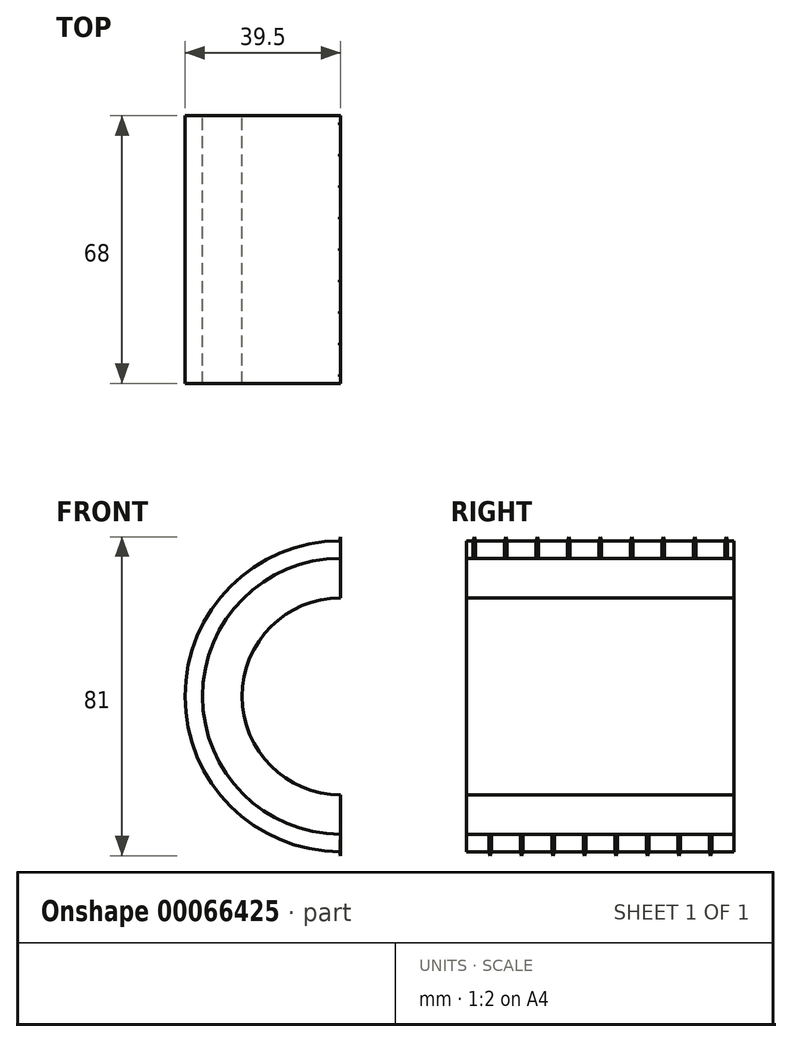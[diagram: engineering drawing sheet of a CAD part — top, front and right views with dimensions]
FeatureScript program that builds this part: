
annotation { "Feature Type Name" : "Feature", "Feature Type Description" : "" }
export const myFeature = defineFeature(function(context is Context, id is Id, definition is map)
    precondition{}
    {
        {
            var Q0;
            Q0=qCreatedBy(makeId("Front.planeOp"),FACE);
            var sketch = newSketch(context, id + "F0", { "sketchPlane" : qUnion([Q0])});
            skCircle(sketch, "E0", {"center": v(0, 0) * mm, "radius": 25.02 * mm});
            skCircle(sketch, "E1", {"center": v(0, 0) * mm, "radius": 35.05 * mm});
            skSolve(sketch);
        }
        {
            var Q0;
            Q0=makeQuery(id+"F0.imprint","IMPRINT",FACE,{"disambiguationData":[TD([[makeQuery(id+"F0.imprint","IMPRINT",EDGE,{"derivedFrom":sQuery(id+"F0.wireOp",EDGE,"E0")}),-1.0]])]});
            extrude(context, id + "F1", {"entities" : qUnion([Q0]), "endBound" : BoundingType.SYMMETRIC, "depth" : 68 * mm});
        }
        {
            var Q0;
            Q0=qCreatedBy(makeId("Front.planeOp"),FACE);
            var sketch = newSketch(context, id + "F2", { "sketchPlane" : qUnion([Q0])});
            skCircle(sketch, "E2.0", {"center": v(0, 0) * mm, "radius": 35.05 * mm});
            skCircle(sketch, "E3", {"center": v(0, 0) * mm, "radius": 39.5 * mm});
            skSolve(sketch);
        }
        {
            var Q0;
            Q0=makeQuery(id+"F2.imprint","IMPRINT",FACE,{"disambiguationData":[TD([[makeQuery(id+"F2.imprint","IMPRINT",EDGE,{"derivedFrom":sQuery(id+"F2.wireOp",EDGE,"E2.0")}),-1.0]])]});
            extrude(context, id + "F3", {"entities" : qUnion([Q0]), "endBound" : BoundingType.SYMMETRIC, "depth" : 68 * mm});
        }
        {
            var Q0;
            Q0=qCreatedBy(makeId("Top.planeOp"),FACE);
            cPlane(context, id + "F4", {"entities" : qUnion([Q0]), "cplaneType" : CPlaneType.OFFSET, "offset" : 70.1 / 2 * mm, "width" : 152.4 * mm, "height" : 152.4 * mm});
        }
        {
            var Q0;
            Q0=qCreatedBy(id+"F4.planeOp",FACE);
            var sketch = newSketch(context, id + "F5", { "sketchPlane" : qUnion([Q0])});
            skCircle(sketch, "E4", {"center": v(0, 0) * mm, "radius": 0.31 * mm});
            skCircle(sketch, "E5.0.1.0", {"center": v(0, 8) * mm, "radius": 0.31 * mm});
            skCircle(sketch, "E5.0.2.0", {"center": v(0, 16) * mm, "radius": 0.31 * mm});
            skCircle(sketch, "E5.0.3.0", {"center": v(0, 24) * mm, "radius": 0.31 * mm});
            skCircle(sketch, "E5.0.4.0", {"center": v(0, 32) * mm, "radius": 0.31 * mm});
            skLineSegment(sketch, "E5.direction1", {"start": v(0, 0) * mm, "end": v(25.4, 0) * mm, "construction": true});
            skLineSegment(sketch, "E5.direction2", {"start": v(0, 0) * mm, "end": v(0, 8) * mm, "construction": true});
            skCircle(sketch, "E6.0.1.0", {"center": v(0, -8) * mm, "radius": 0.31 * mm});
            skCircle(sketch, "E6.0.2.0", {"center": v(0, -16) * mm, "radius": 0.31 * mm});
            skCircle(sketch, "E6.0.3.0", {"center": v(0, -24) * mm, "radius": 0.31 * mm});
            skCircle(sketch, "E6.0.4.0", {"center": v(0, -32) * mm, "radius": 0.31 * mm});
            skLineSegment(sketch, "E6.direction2", {"start": v(0, 0) * mm, "end": v(0, -8) * mm, "construction": true});
            skSolve(sketch);
        }
        {
            var Q0;
            Q0=qSketchRegion(id+"F5",true);
            extrude(context, id + "F6", {"entities" : qUnion([Q0]), "operationType" : NewBodyOperationType.REMOVE, "depth" : 25.4 * mm});
        }
        {
            var Q0;
            Q0=qSketchRegion(id+"F5",true);
            extrude(context, id + "F7", {"entities" : qUnion([Q0]), "depth" : 5.45 * mm});
        }
        {
            var Q0;
            Q0=makeQuery(id+"F7.opExtrude","CAP_EDGE",EDGE,{"disambiguationData":[OSD([sQuery(id+"F5.wireOp",EDGE,"E6.0.4.0")])],"isStart":false});
            var Q1;
            Q1=makeQuery(id+"F7.opExtrude","CAP_EDGE",EDGE,{"disambiguationData":[OSD([sQuery(id+"F5.wireOp",EDGE,"E6.0.3.0")])],"isStart":false});
            var Q2;
            Q2=makeQuery(id+"F7.opExtrude","CAP_EDGE",EDGE,{"disambiguationData":[OSD([sQuery(id+"F5.wireOp",EDGE,"E6.0.2.0")])],"isStart":false});
            var Q3;
            Q3=makeQuery(id+"F7.opExtrude","CAP_EDGE",EDGE,{"disambiguationData":[OSD([sQuery(id+"F5.wireOp",EDGE,"E6.0.1.0")])],"isStart":false});
            var Q4;
            Q4=makeQuery(id+"F7.opExtrude","CAP_EDGE",EDGE,{"disambiguationData":[OSD([sQuery(id+"F5.wireOp",EDGE,"E4")])],"isStart":false});
            var Q5;
            Q5=makeQuery(id+"F7.opExtrude","CAP_EDGE",EDGE,{"disambiguationData":[OSD([sQuery(id+"F5.wireOp",EDGE,"E5.0.1.0")])],"isStart":false});
            var Q6;
            Q6=makeQuery(id+"F7.opExtrude","CAP_EDGE",EDGE,{"disambiguationData":[OSD([sQuery(id+"F5.wireOp",EDGE,"E5.0.2.0")])],"isStart":false});
            var Q7;
            Q7=makeQuery(id+"F7.opExtrude","CAP_EDGE",EDGE,{"disambiguationData":[OSD([sQuery(id+"F5.wireOp",EDGE,"E5.0.3.0")])],"isStart":false});
            var Q8;
            Q8=makeQuery(id+"F7.opExtrude","CAP_EDGE",EDGE,{"disambiguationData":[OSD([sQuery(id+"F5.wireOp",EDGE,"E5.0.4.0")])],"isStart":false});
            chamfer(context, id + "F8", {"entities" : qUnion([Q0, Q1, Q2, Q3, Q4, Q5, Q6, Q7, Q8]), "chamferType" : ChamferType.TWO_OFFSETS, "width1" : 0.31 * mm, "oppositeDirection" : false, "width2" : 1 * mm});
        }
        {
            var Q0;
            Q0=qCreatedBy(makeId("Top.planeOp"),FACE);
            cPlane(context, id + "F9", {"entities" : qUnion([Q0]), "cplaneType" : CPlaneType.OFFSET, "offset" : 70.1 * mm / 2, "oppositeDirection" : true, "width" : 152.4 * mm, "height" : 152.4 * mm});
        }
        {
            var Q0;
            Q0=qCreatedBy(id+"F9.planeOp",FACE);
            var sketch = newSketch(context, id + "F10", { "sketchPlane" : qUnion([Q0])});
            skCircle(sketch, "E7", {"center": v(0, -4) * mm, "radius": 0.31 * mm});
            skCircle(sketch, "E8", {"center": v(0, 4) * mm, "radius": 0.31 * mm});
            skCircle(sketch, "E9.0.1.0", {"center": v(0, -12) * mm, "radius": 0.31 * mm});
            skCircle(sketch, "E9.0.2.0", {"center": v(0, -20) * mm, "radius": 0.31 * mm});
            skCircle(sketch, "E9.0.3.0", {"center": v(0, -28) * mm, "radius": 0.31 * mm});
            skLineSegment(sketch, "E9.direction1", {"start": v(0, -4) * mm, "end": v(20.95, -4) * mm, "construction": true});
            skLineSegment(sketch, "E9.direction2", {"start": v(0, -4) * mm, "end": v(0, -12) * mm, "construction": true});
            skCircle(sketch, "E10.0.1.0", {"center": v(0, 12) * mm, "radius": 0.31 * mm});
            skCircle(sketch, "E10.0.2.0", {"center": v(0, 20) * mm, "radius": 0.31 * mm});
            skCircle(sketch, "E10.0.3.0", {"center": v(0, 28) * mm, "radius": 0.31 * mm});
            skLineSegment(sketch, "E10.direction1", {"start": v(0, 4) * mm, "end": v(25.4, 4) * mm, "construction": true});
            skLineSegment(sketch, "E10.direction2", {"start": v(0, 4) * mm, "end": v(0, 12) * mm, "construction": true});
            skSolve(sketch);
        }
        {
            var Q0;
            Q0=qSketchRegion(id+"F10",true);
            extrude(context, id + "F11", {"entities" : qUnion([Q0]), "operationType" : NewBodyOperationType.REMOVE, "oppositeDirection" : true, "depth" : 25.4 * mm});
        }
        {
            var Q0;
            Q0=qSketchRegion(id+"F10",true);
            extrude(context, id + "F12", {"entities" : qUnion([Q0]), "oppositeDirection" : true, "depth" : 5.45 * mm});
        }
        {
            var Q0;
            Q0=makeQuery(id+"F12.opExtrude","CAP_EDGE",EDGE,{"disambiguationData":[OSD([sQuery(id+"F10.wireOp",EDGE,"E9.0.3.0")])],"isStart":false});
            var Q1;
            Q1=makeQuery(id+"F12.opExtrude","CAP_EDGE",EDGE,{"disambiguationData":[OSD([sQuery(id+"F10.wireOp",EDGE,"E9.0.2.0")])],"isStart":false});
            var Q2;
            Q2=makeQuery(id+"F12.opExtrude","CAP_EDGE",EDGE,{"disambiguationData":[OSD([sQuery(id+"F10.wireOp",EDGE,"E9.0.1.0")])],"isStart":false});
            var Q3;
            Q3=makeQuery(id+"F12.opExtrude","CAP_EDGE",EDGE,{"disambiguationData":[OSD([sQuery(id+"F10.wireOp",EDGE,"E7")])],"isStart":false});
            var Q4;
            Q4=makeQuery(id+"F12.opExtrude","CAP_EDGE",EDGE,{"disambiguationData":[OSD([sQuery(id+"F10.wireOp",EDGE,"E8")])],"isStart":false});
            var Q5;
            Q5=makeQuery(id+"F12.opExtrude","CAP_EDGE",EDGE,{"disambiguationData":[OSD([sQuery(id+"F10.wireOp",EDGE,"E10.0.1.0")])],"isStart":false});
            var Q6;
            Q6=makeQuery(id+"F12.opExtrude","CAP_EDGE",EDGE,{"disambiguationData":[OSD([sQuery(id+"F10.wireOp",EDGE,"E10.0.2.0")])],"isStart":false});
            var Q7;
            Q7=makeQuery(id+"F12.opExtrude","CAP_EDGE",EDGE,{"disambiguationData":[OSD([sQuery(id+"F10.wireOp",EDGE,"E10.0.3.0")])],"isStart":false});
            chamfer(context, id + "F13", {"entities" : qUnion([Q0, Q1, Q2, Q3, Q4, Q5, Q6, Q7]), "chamferType" : ChamferType.TWO_OFFSETS, "width1" : 1 * mm, "oppositeDirection" : false, "width2" : 0.31 * mm, "tangentPropagation" : true});
        }
        {
            var Q0;
            Q0=qCreatedBy(makeId("Front.planeOp"),FACE);
            var sketch = newSketch(context, id + "F14", { "sketchPlane" : qUnion([Q0])});
            skLineSegment(sketch, "E11.bottom", {"start": v(0, -52.11) * mm, "end": v(45.42, -52.11) * mm});
            skLineSegment(sketch, "E11.top", {"start": v(0, 55.13) * mm, "end": v(45.42, 55.13) * mm});
            skLineSegment(sketch, "E11.left", {"start": v(0, -52.11) * mm, "end": v(0, 55.13) * mm});
            skLineSegment(sketch, "E11.right", {"start": v(45.42, -52.11) * mm, "end": v(45.42, 55.13) * mm});
            skSolve(sketch);
        }
        {
            var Q0;
            Q0=makeQuery(id+"F14.imprint","IMPRINT",FACE,{"disambiguationData":[TD([[makeQuery(id+"F14.imprint","IMPRINT",EDGE,{"derivedFrom":sQuery(id+"F14.wireOp",EDGE,"E11.bottom")}),1.0]])]});
            extrude(context, id + "F15", {"entities" : qUnion([Q0]), "operationType" : NewBodyOperationType.REMOVE, "endBound" : BoundingType.THROUGH_ALL, "oppositeDirection" : true, "depth" : 25.4 * mm, "hasSecondDirection" : true, "secondDirectionBound" : SecondDirectionBoundingType.THROUGH_ALL, "secondDirectionOppositeDirection" : false, "secondDirectionDepth" : 25.4 * mm});
        }
    });
